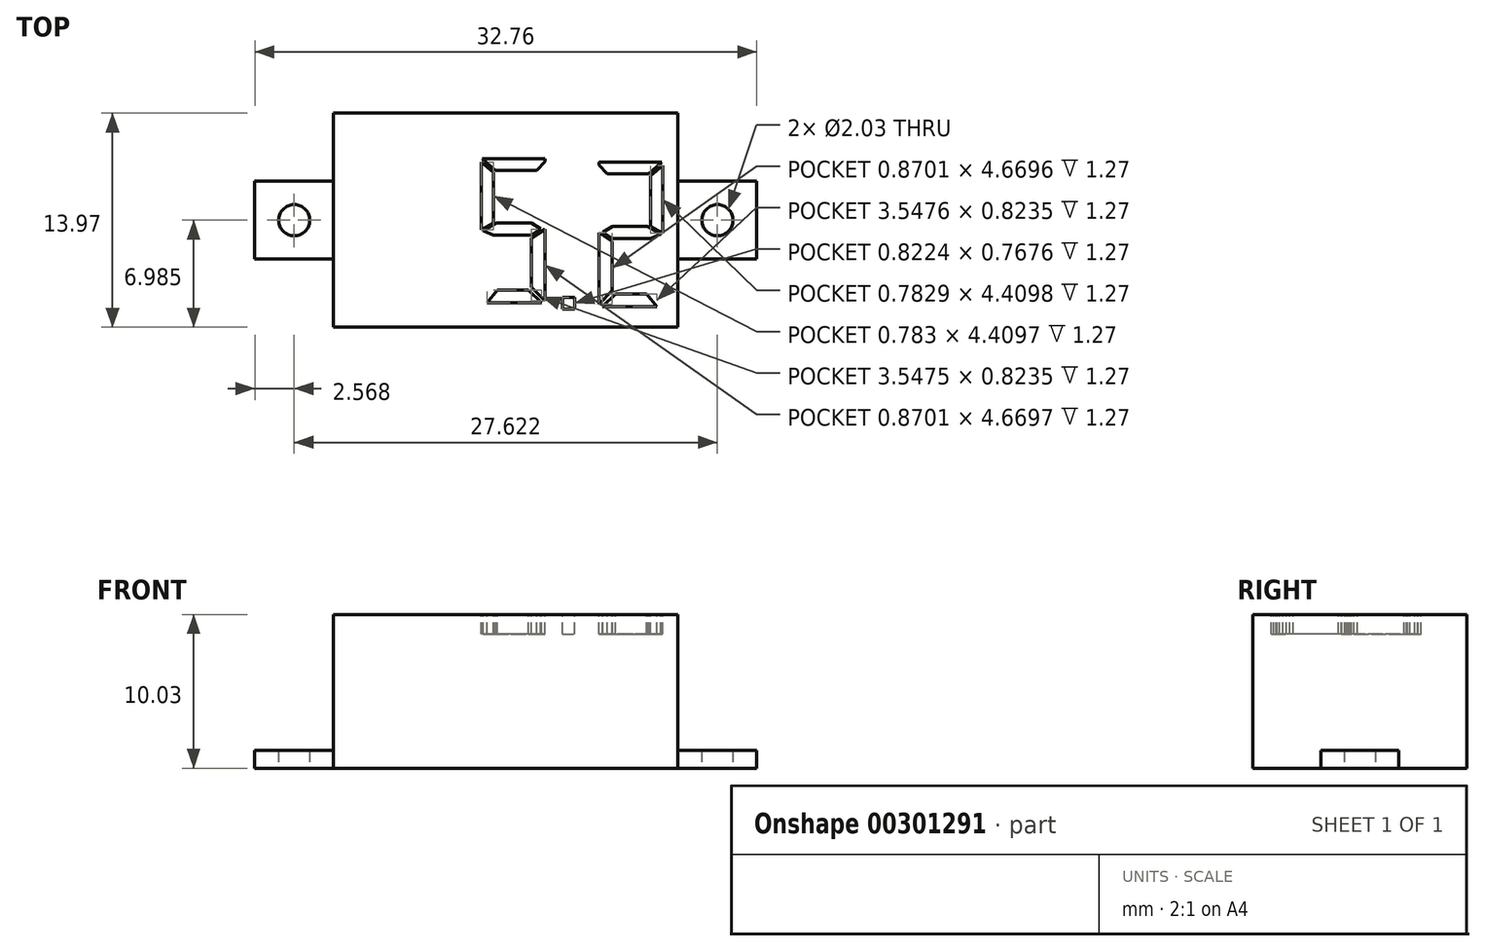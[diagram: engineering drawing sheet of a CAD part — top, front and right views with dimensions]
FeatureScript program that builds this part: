
annotation { "Feature Type Name" : "Feature", "Feature Type Description" : "" }
export const myFeature = defineFeature(function(context is Context, id is Id, definition is map)
    precondition{}
    {
        {
            var Q0;
            Q0=qCreatedBy(makeId("Top.planeOp"),FACE);
            var sketch = newSketch(context, id + "F0", { "sketchPlane" : qUnion([Q0])});
            skLineSegment(sketch, "E0.bottom", {"start": v(0, 0) * mm, "end": v(22.48, 0) * mm});
            skLineSegment(sketch, "E0.top", {"start": v(0, 13.97) * mm, "end": v(22.48, 13.97) * mm});
            skLineSegment(sketch, "E0.left", {"start": v(0, 0) * mm, "end": v(0, 13.97) * mm});
            skLineSegment(sketch, "E0.right", {"start": v(22.48, 0) * mm, "end": v(22.48, 13.97) * mm});
            skSolve(sketch);
        }
        {
            var Q0;
            Q0 = qSketchRegion(id + "F0", true);
            extrude(context, id + "F1", {"entities" : qUnion([Q0]), "depth" : 10.03 * mm});
        }
        {
            var Q0;
            Q0=makeQuery(id+"F1.opExtrude","CAP_FACE",FACE,{"disambiguationData":[OSD([sQuery(id+"F0.wireOp",EDGE,"E0.bottom"),sQuery(id+"F0.wireOp",EDGE,"E0.top"),sQuery(id+"F0.wireOp",EDGE,"E0.left"),sQuery(id+"F0.wireOp",EDGE,"E0.right")])],"isStart":true});
            var sketch = newSketch(context, id + "F2", { "sketchPlane" : qUnion([Q0])});
            skLineSegment(sketch, "E1.bottom", {"start": v(0, -4.44) * mm, "end": v(-5.14, -4.44) * mm});
            skLineSegment(sketch, "E1.top", {"start": v(0, -9.53) * mm, "end": v(-5.14, -9.53) * mm});
            skLineSegment(sketch, "E1.left", {"start": v(0, -4.44) * mm, "end": v(0, -9.53) * mm});
            skLineSegment(sketch, "E1.right", {"start": v(-5.14, -4.44) * mm, "end": v(-5.14, -9.53) * mm});
            skPoint(sketch, "E2", {"position": v(0, -6.99) * mm});
            skCircle(sketch, "E3", {"center": v(-2.57, -6.99) * mm, "radius": 1.02 * mm});
            skLineSegment(sketch, "E4", {"start": v(-2.57, -4.44) * mm, "end": v(-2.57, -9.53) * mm, "construction": true});
            skLineSegment(sketch, "E5", {"start": v(-5.14, -6.99) * mm, "end": v(0, -6.99) * mm, "construction": true});
            skLineSegment(sketch, "E6", {"start": v(11.24, 0) * mm, "end": v(11.24, -13.97) * mm, "construction": true});
            skLineSegment(sketch, "E7.MirrorCS", {"start": v(22.48, -4.44) * mm, "end": v(22.48, -9.53) * mm});
            skPoint(sketch, "E8.MirrorP", {"position": v(22.48, -6.99) * mm});
            skLineSegment(sketch, "E9.MirrorCS", {"start": v(27.62, -6.99) * mm, "end": v(22.48, -6.99) * mm, "construction": true});
            skLineSegment(sketch, "E10.MirrorCS", {"start": v(25.05, -4.44) * mm, "end": v(25.05, -9.53) * mm, "construction": true});
            skCircle(sketch, "E11.MirrorC", {"center": v(25.05, -6.99) * mm, "radius": 1.02 * mm});
            skLineSegment(sketch, "E12.MirrorCS", {"start": v(27.62, -4.44) * mm, "end": v(27.62, -9.53) * mm});
            skLineSegment(sketch, "E13.MirrorCS", {"start": v(22.48, -9.53) * mm, "end": v(27.62, -9.53) * mm});
            skLineSegment(sketch, "E14.MirrorCS", {"start": v(22.48, -4.44) * mm, "end": v(27.62, -4.44) * mm});
            skSolve(sketch);
        }
        {
            var Q0;
            Q0 = qSketchRegion(id + "F2", true);
            extrude(context, id + "F3", {"entities" : qUnion([Q0]), "operationType" : NewBodyOperationType.ADD, "oppositeDirection" : true, "depth" : 1.17 * mm});
        }
        {
            var Q0;
            Q0=makeQuery(id+"F1.opExtrude","CAP_FACE",FACE,{"disambiguationData":[OSD([sQuery(id+"F0.wireOp",EDGE,"E0.bottom"),sQuery(id+"F0.wireOp",EDGE,"E0.top"),sQuery(id+"F0.wireOp",EDGE,"E0.left"),sQuery(id+"F0.wireOp",EDGE,"E0.right")])],"isStart":false});
            var sketch = newSketch(context, id + "F4", { "sketchPlane" : qUnion([Q0])});
            skLineSegment(sketch, "E15", {"start": v(13.79, 10.98) * mm, "end": v(9.7, 10.98) * mm});
            skLineSegment(sketch, "E16", {"start": v(9.64, 10.78) * mm, "end": v(9.64, 6.37) * mm});
            skLineSegment(sketch, "E17", {"start": v(10.43, 6) * mm, "end": v(12.92, 6) * mm});
            skLineSegment(sketch, "E18", {"start": v(13.79, 6) * mm, "end": v(13.79, 1.74) * mm});
            skLineSegment(sketch, "E19", {"start": v(13.56, 1.58) * mm, "end": v(10.01, 1.58) * mm});
            skLineSegment(sketch, "E20", {"start": v(10.67, 2.4) * mm, "end": v(12.72, 2.4) * mm});
            skLineSegment(sketch, "E21", {"start": v(12.92, 5.81) * mm, "end": v(12.92, 2.63) * mm});
            skLineSegment(sketch, "E22", {"start": v(13.79, 6) * mm, "end": v(13.79, 6.4) * mm});
            skLineSegment(sketch, "E23", {"start": v(12.9, 6.8) * mm, "end": v(10.65, 6.8) * mm});
            skLineSegment(sketch, "E24", {"start": v(10.43, 6.8) * mm, "end": v(10.43, 10.1) * mm});
            skLineSegment(sketch, "E25", {"start": v(10.55, 10.24) * mm, "end": v(13.26, 10.24) * mm});
            skLineSegment(sketch, "E26", {"start": v(13.79, 10.8) * mm, "end": v(13.79, 10.98) * mm});
            skLineSegment(sketch, "E27.bottom", {"start": v(14.93, 1.2) * mm, "end": v(15.75, 1.2) * mm});
            skLineSegment(sketch, "E27.top", {"start": v(14.93, 1.96) * mm, "end": v(15.75, 1.96) * mm});
            skLineSegment(sketch, "E27.left", {"start": v(14.93, 1.2) * mm, "end": v(14.93, 1.96) * mm});
            skLineSegment(sketch, "E27.right", {"start": v(15.75, 1.2) * mm, "end": v(15.75, 1.96) * mm});
            skLineSegment(sketch, "E28", {"start": v(10.43, 10.1) * mm, "end": v(9.64, 10.78) * mm});
            skLineSegment(sketch, "E29", {"start": v(10.55, 10.24) * mm, "end": v(9.7, 10.98) * mm});
            skLineSegment(sketch, "E30", {"start": v(13.26, 10.24) * mm, "end": v(13.79, 10.8) * mm});
            skLineSegment(sketch, "E31", {"start": v(10.43, 6.8) * mm, "end": v(9.64, 6.37) * mm});
            skLineSegment(sketch, "E32", {"start": v(9.77, 6.3) * mm, "end": v(10.43, 6) * mm});
            skLineSegment(sketch, "E33", {"start": v(13.79, 6.4) * mm, "end": v(12.92, 5.81) * mm});
            skLineSegment(sketch, "E34", {"start": v(12.9, 6.8) * mm, "end": v(13.52, 6.44) * mm});
            skLineSegment(sketch, "E35", {"start": v(12.92, 6) * mm, "end": v(13.52, 6.44) * mm});
            skLineSegment(sketch, "E36", {"start": v(12.92, 2.63) * mm, "end": v(13.79, 1.74) * mm});
            skLineSegment(sketch, "E37", {"start": v(12.72, 2.4) * mm, "end": v(13.56, 1.58) * mm});
            skLineSegment(sketch, "E38", {"start": v(10.01, 1.58) * mm, "end": v(10.67, 2.4) * mm});
            skPoint(sketch, "E39.trimOffspring.end.orphan", {"position": v(13.79, 2.4) * mm});
            skPoint(sketch, "E40.orphan", {"position": v(13.79, 6.8) * mm});
            skLineSegment(sketch, "E41", {"start": v(10.65, 6.8) * mm, "end": v(9.77, 6.3) * mm});
            skLineSegment(sketch, "E42.MirrorCS", {"start": v(18.22, 6.58) * mm, "end": v(17.59, 6.21) * mm});
            skLineSegment(sketch, "E43.MirrorCS", {"start": v(21.34, 6.08) * mm, "end": v(20.68, 5.78) * mm});
            skLineSegment(sketch, "E44.MirrorCS", {"start": v(17.85, 10.02) * mm, "end": v(17.32, 10.57) * mm});
            skLineSegment(sketch, "E45.MirrorCS", {"start": v(20.46, 6.58) * mm, "end": v(21.34, 6.08) * mm});
            skLineSegment(sketch, "E46.MirrorCS", {"start": v(20.68, 6.58) * mm, "end": v(21.47, 6.14) * mm});
            skLineSegment(sketch, "E47.MirrorCS", {"start": v(17.32, 10.57) * mm, "end": v(17.32, 10.76) * mm});
            skLineSegment(sketch, "E48.MirrorCS", {"start": v(18.2, 5.78) * mm, "end": v(17.59, 6.21) * mm});
            skLineSegment(sketch, "E49.MirrorCS", {"start": v(18.2, 2.4) * mm, "end": v(17.32, 1.51) * mm});
            skLineSegment(sketch, "E50.MirrorCS", {"start": v(20.44, 2.18) * mm, "end": v(18.4, 2.18) * mm});
            skLineSegment(sketch, "E51.MirrorCS", {"start": v(20.68, 6.58) * mm, "end": v(20.68, 9.88) * mm});
            skLineSegment(sketch, "E52.MirrorCS", {"start": v(20.68, 5.78) * mm, "end": v(18.2, 5.78) * mm});
            skLineSegment(sketch, "E53.MirrorCS", {"start": v(20.68, 9.88) * mm, "end": v(21.47, 10.55) * mm});
            skLineSegment(sketch, "E54.MirrorCS", {"start": v(17.32, 10.76) * mm, "end": v(21.42, 10.76) * mm});
            skLineSegment(sketch, "E55.MirrorCS", {"start": v(18.4, 2.18) * mm, "end": v(17.55, 1.36) * mm});
            skLineSegment(sketch, "E56.MirrorCS", {"start": v(17.55, 1.36) * mm, "end": v(21.1, 1.36) * mm});
            skLineSegment(sketch, "E57.MirrorCS", {"start": v(21.47, 10.55) * mm, "end": v(21.47, 6.14) * mm});
            skLineSegment(sketch, "E58.MirrorCS", {"start": v(21.1, 1.36) * mm, "end": v(20.44, 2.18) * mm});
            skLineSegment(sketch, "E59.MirrorCS", {"start": v(20.56, 10.02) * mm, "end": v(21.42, 10.76) * mm});
            skLineSegment(sketch, "E60.MirrorCS", {"start": v(18.22, 6.58) * mm, "end": v(20.46, 6.58) * mm});
            skPoint(sketch, "E61.MirrorP", {"position": v(17.32, 2.18) * mm});
            skLineSegment(sketch, "E62.MirrorCS", {"start": v(17.32, 6.18) * mm, "end": v(18.2, 5.59) * mm});
            skLineSegment(sketch, "E63.MirrorCS", {"start": v(20.56, 10.02) * mm, "end": v(17.85, 10.02) * mm});
            skPoint(sketch, "E64.MirrorP", {"position": v(17.32, 6.58) * mm});
            skLineSegment(sketch, "E65.MirrorCS", {"start": v(17.32, 6.18) * mm, "end": v(17.32, 1.51) * mm});
            skLineSegment(sketch, "E66.MirrorCS", {"start": v(18.2, 5.59) * mm, "end": v(18.2, 2.4) * mm});
            skSolve(sketch);
        }
        {
            var Q0;
            Q0 = qSketchRegion(id + "F4", true);
            extrude(context, id + "F5", {"entities" : qUnion([Q0]), "operationType" : NewBodyOperationType.REMOVE, "oppositeDirection" : true, "depth" : 1.27 * mm});
        }
    });
